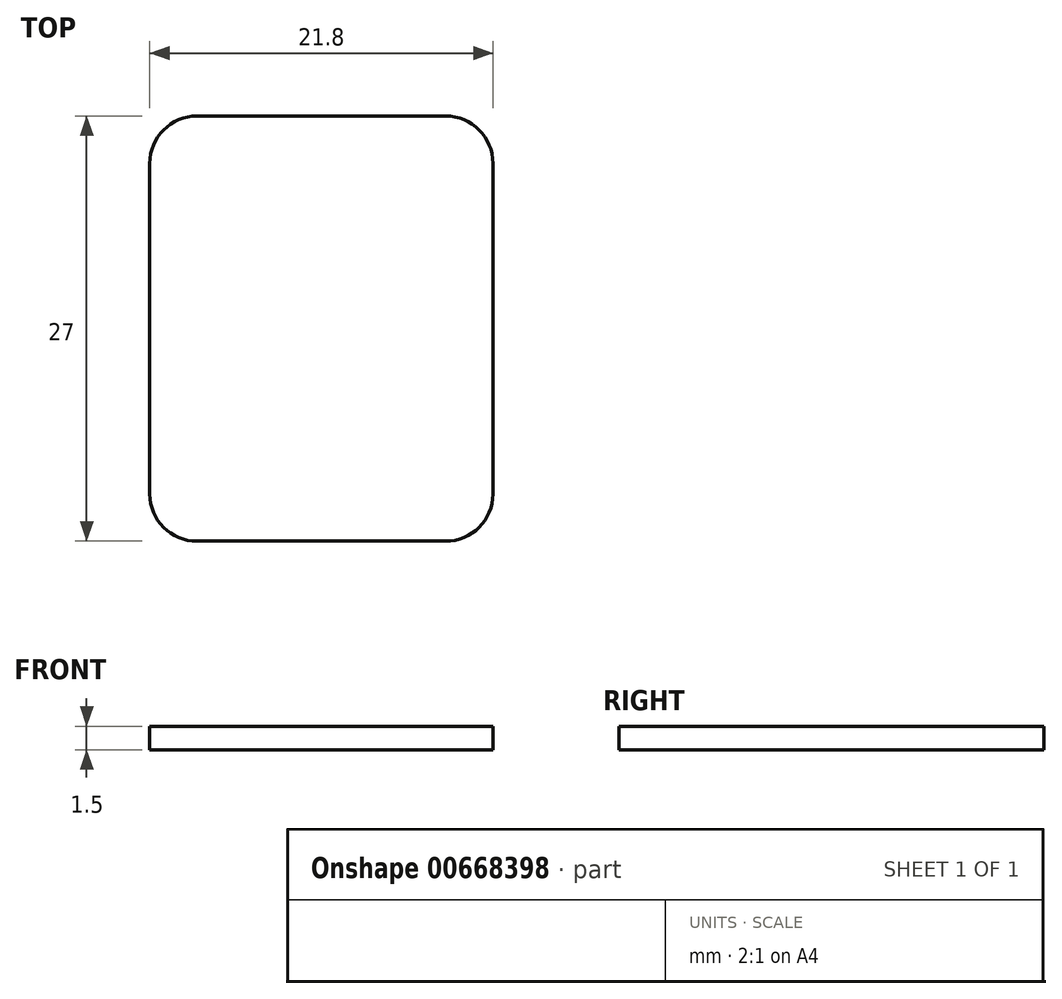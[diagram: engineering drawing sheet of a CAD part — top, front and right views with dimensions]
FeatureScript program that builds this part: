
annotation { "Feature Type Name" : "Feature", "Feature Type Description" : "" }
export const myFeature = defineFeature(function(context is Context, id is Id, definition is map)
    precondition{}
    {
        {
            var Q0;
            Q0=qCreatedBy(makeId("Top.planeOp"),FACE);
            var sketch = newSketch(context, id + "F0", { "sketchPlane" : qUnion([Q0])});
            skLineSegment(sketch, "E0.bottom", {"start": v(3, 0) * mm, "end": v(18.8, 0) * mm});
            skLineSegment(sketch, "E0.top", {"start": v(3, 27) * mm, "end": v(18.8, 27) * mm});
            skLineSegment(sketch, "E0.left", {"start": v(0, 3) * mm, "end": v(0, 24) * mm});
            skLineSegment(sketch, "E0.right", {"start": v(21.8, 3) * mm, "end": v(21.8, 24) * mm});
            skPoint(sketch, "E1.visualSharp", {"position": v(0, 27) * mm});
            skArc(sketch, "E1.filletArc", {"start": v(3, 27) * mm, "mid": v(0.88, 26.12) * mm, "end": v(0, 24) * mm});
            skPoint(sketch, "E2.visualSharp", {"position": v(21.8, 27) * mm});
            skArc(sketch, "E2.filletArc", {"start": v(21.8, 24) * mm, "mid": v(20.92, 26.12) * mm, "end": v(18.8, 27) * mm});
            skPoint(sketch, "E3.visualSharp", {"position": v(21.8, 0) * mm});
            skArc(sketch, "E3.filletArc", {"start": v(18.8, 0) * mm, "mid": v(20.92, 0.88) * mm, "end": v(21.8, 3) * mm});
            skPoint(sketch, "E4.visualSharp", {"position": v(0, 0) * mm});
            skArc(sketch, "E4.filletArc", {"start": v(0, 3) * mm, "mid": v(0.88, 0.88) * mm, "end": v(3, 0) * mm});
            skSolve(sketch);
        }
        {
            var Q0;
            Q0 = qSketchRegion(id + "F0", true);
            extrude(context, id + "F1", {"entities" : qUnion([Q0]), "depth" : 1.5 * mm, "offsetDistance" : 25 * mm});
        }
    });
